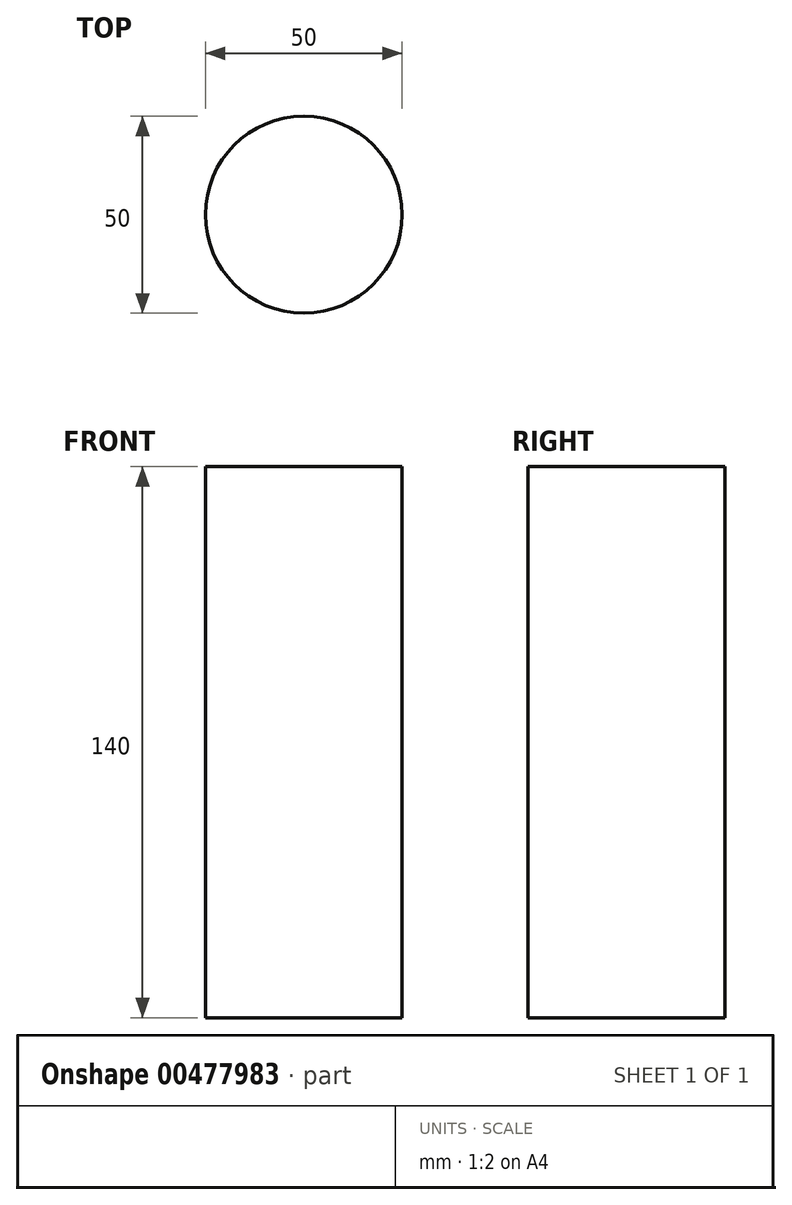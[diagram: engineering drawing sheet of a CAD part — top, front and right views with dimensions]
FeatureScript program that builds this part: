
annotation { "Feature Type Name" : "Feature", "Feature Type Description" : "" }
export const myFeature = defineFeature(function(context is Context, id is Id, definition is map)
    precondition{}
    {
        {
            var Q0;
            Q0=qCreatedBy(makeId("Top.planeOp"),FACE);
            var sketch = newSketch(context, id + "F0", { "sketchPlane" : qUnion([Q0])});
            skCircle(sketch, "E0", {"center": v(0, 0) * mm, "radius": 25 * mm});
            skSolve(sketch);
        }
        {
            var Q0;
            Q0=sQuery(id+"F0.wireOp",EDGE,"E0");
            extrude(context, id + "F1", {"bodyType" : ToolBodyType.SURFACE, "surfaceEntities" : qUnion([Q0]), "depth" : 140 * mm});
        }
    });
